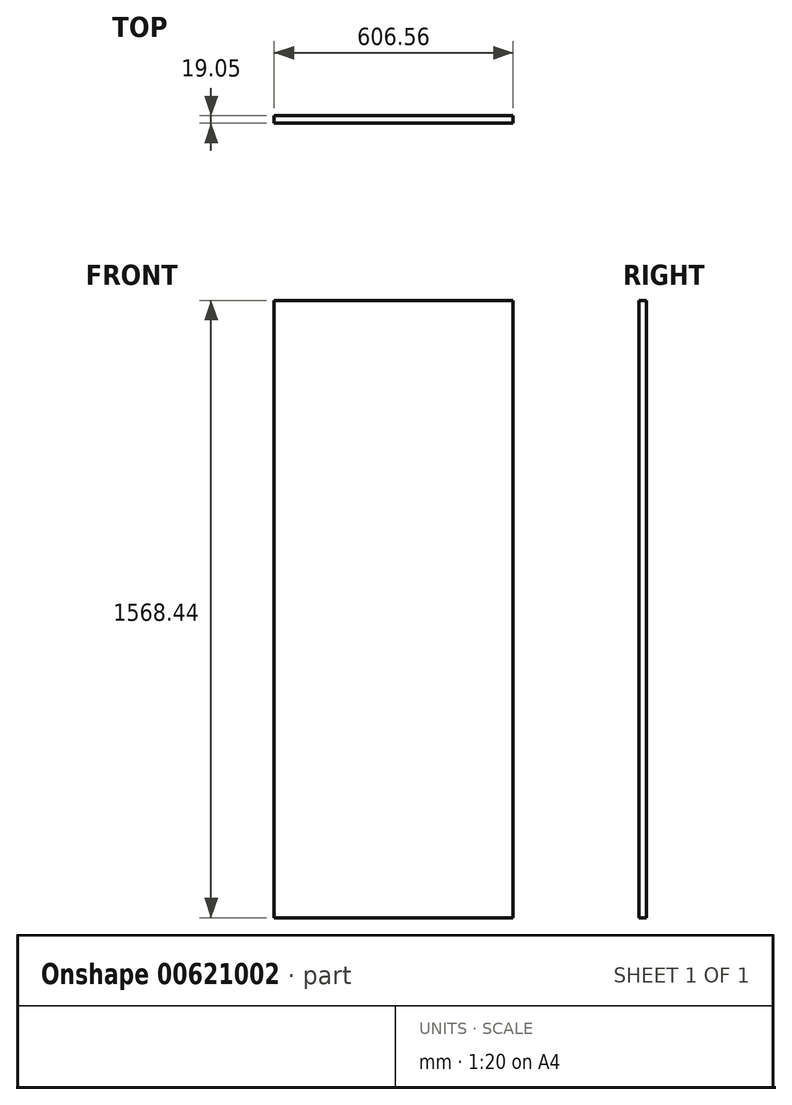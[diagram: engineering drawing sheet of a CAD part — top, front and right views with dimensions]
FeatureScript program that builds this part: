
annotation { "Feature Type Name" : "Feature", "Feature Type Description" : "" }
export const myFeature = defineFeature(function(context is Context, id is Id, definition is map)
    precondition{}
    {
        {
            var Q0;
            Q0=qCreatedBy(makeId("Front.planeOp"),FACE);
            var sketch = newSketch(context, id + "F0", { "sketchPlane" : qUnion([Q0])});
            skLineSegment(sketch, "E0.bottom", {"start": v(-303.28, 784.23) * mm, "end": v(303.28, 784.23) * mm});
            skLineSegment(sketch, "E0.top", {"start": v(-303.28, -784.23) * mm, "end": v(303.28, -784.23) * mm});
            skLineSegment(sketch, "E0.left", {"start": v(-303.28, 784.23) * mm, "end": v(-303.28, -784.23) * mm});
            skLineSegment(sketch, "E0.right", {"start": v(303.28, 784.23) * mm, "end": v(303.28, -784.23) * mm});
            skPoint(sketch, "E0.middle", {"position": v(0, 0) * mm});
            skSolve(sketch);
        }
        {
            var Q0;
            Q0=makeQuery(id+"F0.imprint","IMPRINT",FACE,{"disambiguationData":[TD([[makeQuery(id+"F0.imprint","IMPRINT",EDGE,{"derivedFrom":sQuery(id+"F0.wireOp",EDGE,"E0.bottom")}),-1.0]])]});
            extrude(context, id + "F1", {"entities" : qUnion([Q0]), "depth" : 19.05 * mm, "offsetDistance" : 25.4 * mm});
        }
    });
